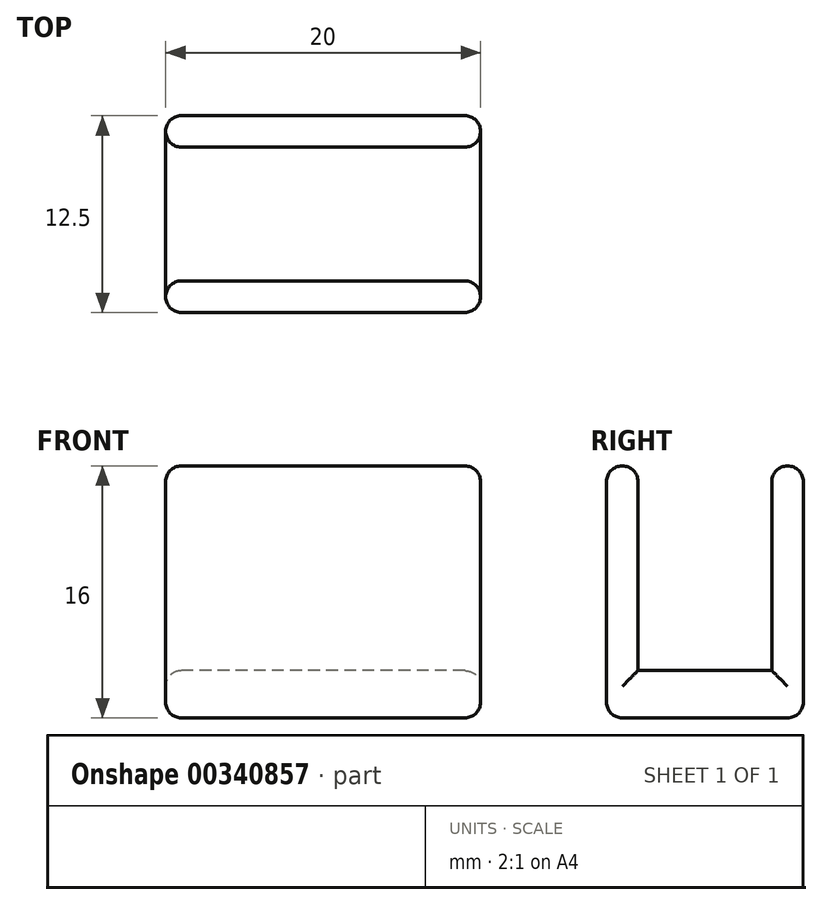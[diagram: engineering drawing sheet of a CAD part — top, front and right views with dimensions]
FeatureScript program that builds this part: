
annotation { "Feature Type Name" : "Feature", "Feature Type Description" : "" }
export const myFeature = defineFeature(function(context is Context, id is Id, definition is map)
    precondition{}
    {
        {
            var Q0;
            Q0=qCreatedBy(makeId("Top.planeOp"),FACE);
            var sketch = newSketch(context, id + "F0", { "sketchPlane" : qUnion([Q0])});
            skLineSegment(sketch, "E0.bottom", {"start": v(0, 0) * mm, "end": v(20, 0) * mm});
            skLineSegment(sketch, "E0.top", {"start": v(0, -12.5) * mm, "end": v(20, -12.5) * mm});
            skLineSegment(sketch, "E0.left", {"start": v(0, 0) * mm, "end": v(0, -12.5) * mm});
            skLineSegment(sketch, "E0.right", {"start": v(20, 0) * mm, "end": v(20, -12.5) * mm});
            skLineSegment(sketch, "E1.bottom", {"start": v(0, -2) * mm, "end": v(20, -2) * mm});
            skLineSegment(sketch, "E1.top", {"start": v(0, -10.5) * mm, "end": v(20, -10.5) * mm});
            skLineSegment(sketch, "E1.left", {"start": v(0, -2) * mm, "end": v(0, -10.5) * mm});
            skLineSegment(sketch, "E1.right", {"start": v(20, -2) * mm, "end": v(20, -10.5) * mm});
            skSolve(sketch);
        }
        {
            var Q0;
            Q0 = qSketchRegion(id + "F0", true);
            extrude(context, id + "F1", {"entities" : qUnion([Q0]), "depth" : 3 * mm});
        }
        {
            var Q0;
            {var subQ0=sQuery(id+"F0.wireOp",EDGE,"E0.bottom");Q0=makeQuery(id+"F0.imprint","IMPRINT",FACE,{"disambiguationData":[TD([[makeQuery(id+"F0.imprint","IMPRINT",EDGE,{"derivedFrom":subQ0}),-1.0]])]});}
            var Q1;
            {var subQ0=sQuery(id+"F0.wireOp",EDGE,"E0.top");Q1=makeQuery(id+"F0.imprint","IMPRINT",FACE,{"disambiguationData":[TD([[makeQuery(id+"F0.imprint","IMPRINT",EDGE,{"derivedFrom":subQ0}),1.0]])]});}
            extrude(context, id + "F2", {"entities" : qUnion([Q0, Q1]), "operationType" : NewBodyOperationType.ADD, "depth" : 16 * mm});
        }
        {
            var Q0;
            Q0=makeQuery(id+"F2.opExtrude","CAP_FACE",FACE,{"disambiguationData":[OSD([sQuery(id+"F0.wireOp",EDGE,"E0.bottom"),sQuery(id+"F0.wireOp",EDGE,"E0.left"),sQuery(id+"F0.wireOp",EDGE,"E0.right"),sQuery(id+"F0.wireOp",EDGE,"E1.bottom")])],"isStart":false});
            var Q1;
            Q1=makeQuery(id+"F2.opExtrude","CAP_FACE",FACE,{"disambiguationData":[OSD([sQuery(id+"F0.wireOp",EDGE,"E0.top"),sQuery(id+"F0.wireOp",EDGE,"E0.left"),sQuery(id+"F0.wireOp",EDGE,"E0.right"),sQuery(id+"F0.wireOp",EDGE,"E1.top")])],"isStart":false});
            var Q2;
            {var subQ0=sQuery(id+"F0.wireOp",EDGE,"E0.left");var subQ1=sQuery(id+"F0.wireOp",EDGE,"E1.left");Q2=makeQuery(id+"F2.boolean.opBoolean","MERGE",FACE,{"derivedFrom":[makeQuery(id+"F1.opExtrude","SWEPT_FACE",FACE,{"disambiguationData":[OSD([subQ0,subQ1])]}),makeQuery(id+"F2.opExtrude","SWEPT_FACE",FACE,{"disambiguationData":[OSD([subQ0]),TDD([makeQuery(id+"F0.imprint","IMPRINT",EDGE,{"disambiguationData":[TD([[makeQuery(id+"F0.imprint","INTERSECT",VERTEX,{"derivedFrom":[sQuery(id+"F0.wireOp",EDGE,"E0.bottom"),subQ0]}),-1.0]])],"derivedFrom":subQ0})])]}),makeQuery(id+"F2.opExtrude","SWEPT_FACE",FACE,{"disambiguationData":[OSD([subQ0]),TDD([makeQuery(id+"F0.imprint","IMPRINT",EDGE,{"disambiguationData":[TD([[makeQuery(id+"F0.imprint","INTERSECT",VERTEX,{"derivedFrom":[sQuery(id+"F0.wireOp",EDGE,"E0.top"),subQ0]}),1.0]])],"derivedFrom":subQ0})])]})]});}
            var Q3;
            {var subQ0=sQuery(id+"F0.wireOp",EDGE,"E0.right");var subQ1=sQuery(id+"F0.wireOp",EDGE,"E1.right");Q3=makeQuery(id+"F2.boolean.opBoolean","MERGE",FACE,{"derivedFrom":[makeQuery(id+"F1.opExtrude","SWEPT_FACE",FACE,{"disambiguationData":[OSD([subQ0,subQ1])]}),makeQuery(id+"F2.opExtrude","SWEPT_FACE",FACE,{"disambiguationData":[OSD([subQ0]),TDD([makeQuery(id+"F0.imprint","IMPRINT",EDGE,{"disambiguationData":[TD([[makeQuery(id+"F0.imprint","INTERSECT",VERTEX,{"derivedFrom":[sQuery(id+"F0.wireOp",EDGE,"E0.bottom"),subQ0]}),-1.0]])],"derivedFrom":subQ0})])]}),makeQuery(id+"F2.opExtrude","SWEPT_FACE",FACE,{"disambiguationData":[OSD([subQ0]),TDD([makeQuery(id+"F0.imprint","IMPRINT",EDGE,{"disambiguationData":[TD([[makeQuery(id+"F0.imprint","INTERSECT",VERTEX,{"derivedFrom":[sQuery(id+"F0.wireOp",EDGE,"E0.top"),subQ0]}),1.0]])],"derivedFrom":subQ0})])]})]});}
            var Q4;
            Q4=makeQuery(id+"F1.opExtrude","CAP_FACE",FACE,{"disambiguationData":[OSD([sQuery(id+"F0.wireOp",EDGE,"E0.bottom"),sQuery(id+"F0.wireOp",EDGE,"E0.top"),sQuery(id+"F0.wireOp",EDGE,"E0.left"),sQuery(id+"F0.wireOp",EDGE,"E0.right"),sQuery(id+"F0.wireOp",EDGE,"E1.left"),sQuery(id+"F0.wireOp",EDGE,"E1.right")])],"isStart":true});
            fillet(context, id + "F3", {"entities" : qUnion([Q0, Q1, Q2, Q3, Q4]), "radius" : 1 * mm, "tangentPropagation" : true, "allowEdgeOverflow" : false});
        }
    });
